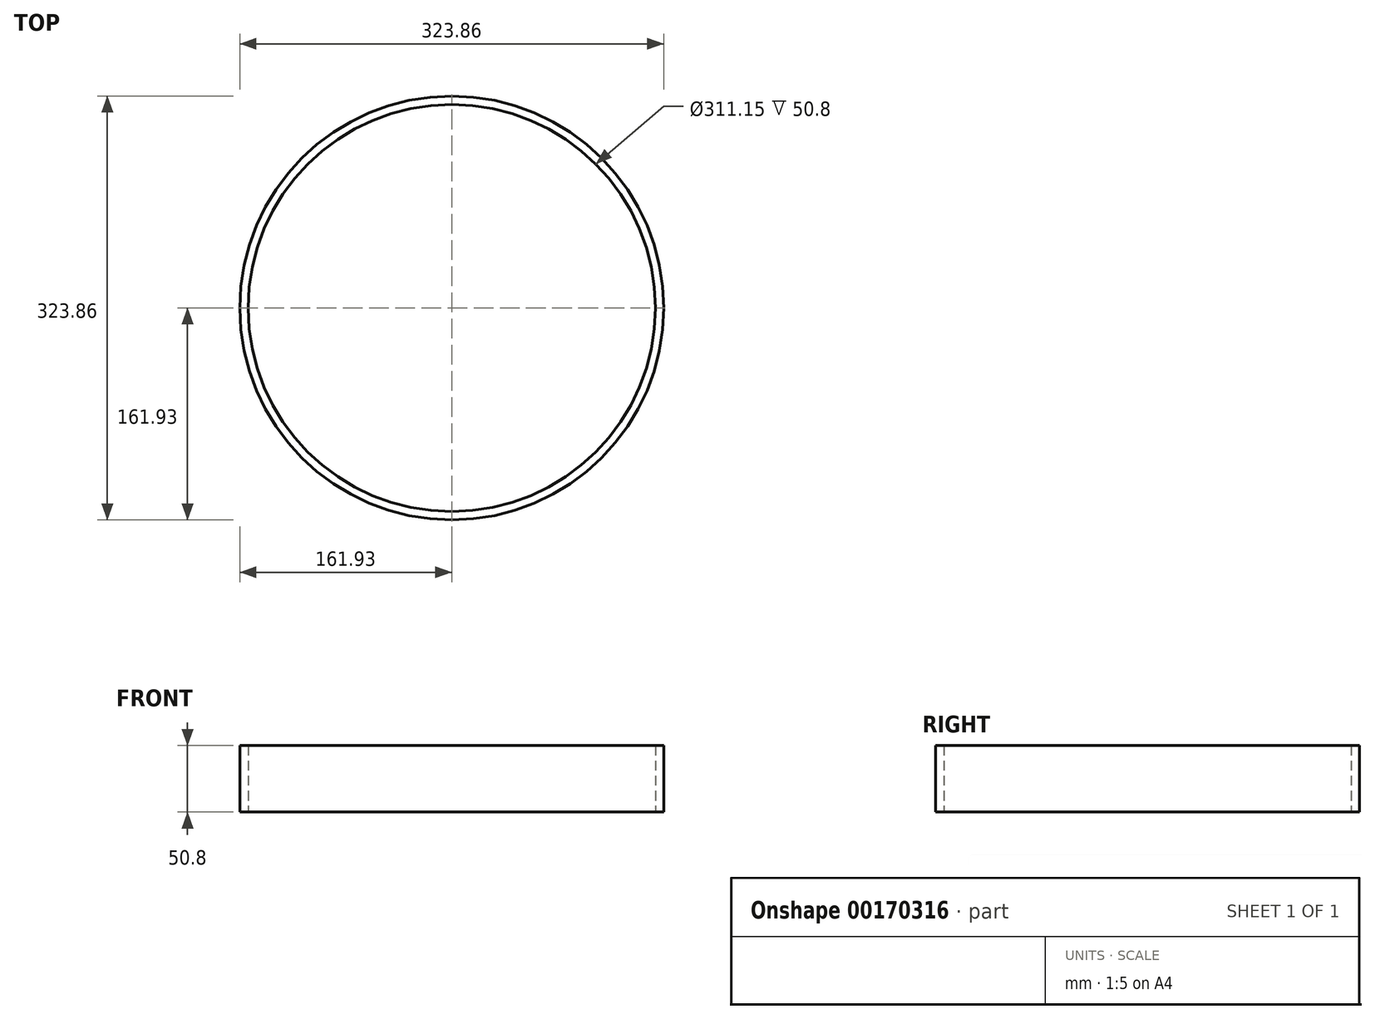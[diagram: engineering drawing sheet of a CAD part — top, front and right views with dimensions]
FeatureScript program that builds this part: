
annotation { "Feature Type Name" : "Feature", "Feature Type Description" : "" }
export const myFeature = defineFeature(function(context is Context, id is Id, definition is map)
    precondition{}
    {
        {
            var Q0;
            Q0=qCreatedBy(makeId("Top.planeOp"),FACE);
            var sketch = newSketch(context, id + "F0", { "sketchPlane" : qUnion([Q0])});
            skCircle(sketch, "E0", {"center": v(0, 0) * mm, "radius": 161.93 * mm});
            skCircle(sketch, "E1.0", {"center": v(0, 0) * mm, "radius": 155.58 * mm});
            skSolve(sketch);
        }
        {
            var Q0;
            Q0=makeQuery(id+"F0.imprint","IMPRINT",FACE,{"disambiguationData":[TD([[makeQuery(id+"F0.imprint","IMPRINT",EDGE,{"derivedFrom":sQuery(id+"F0.wireOp",EDGE,"E1.0")}),-1.0]])]});
            extrude(context, id + "F1", {"entities" : qUnion([Q0]), "depth" : 50.8 * mm});
        }
    });
